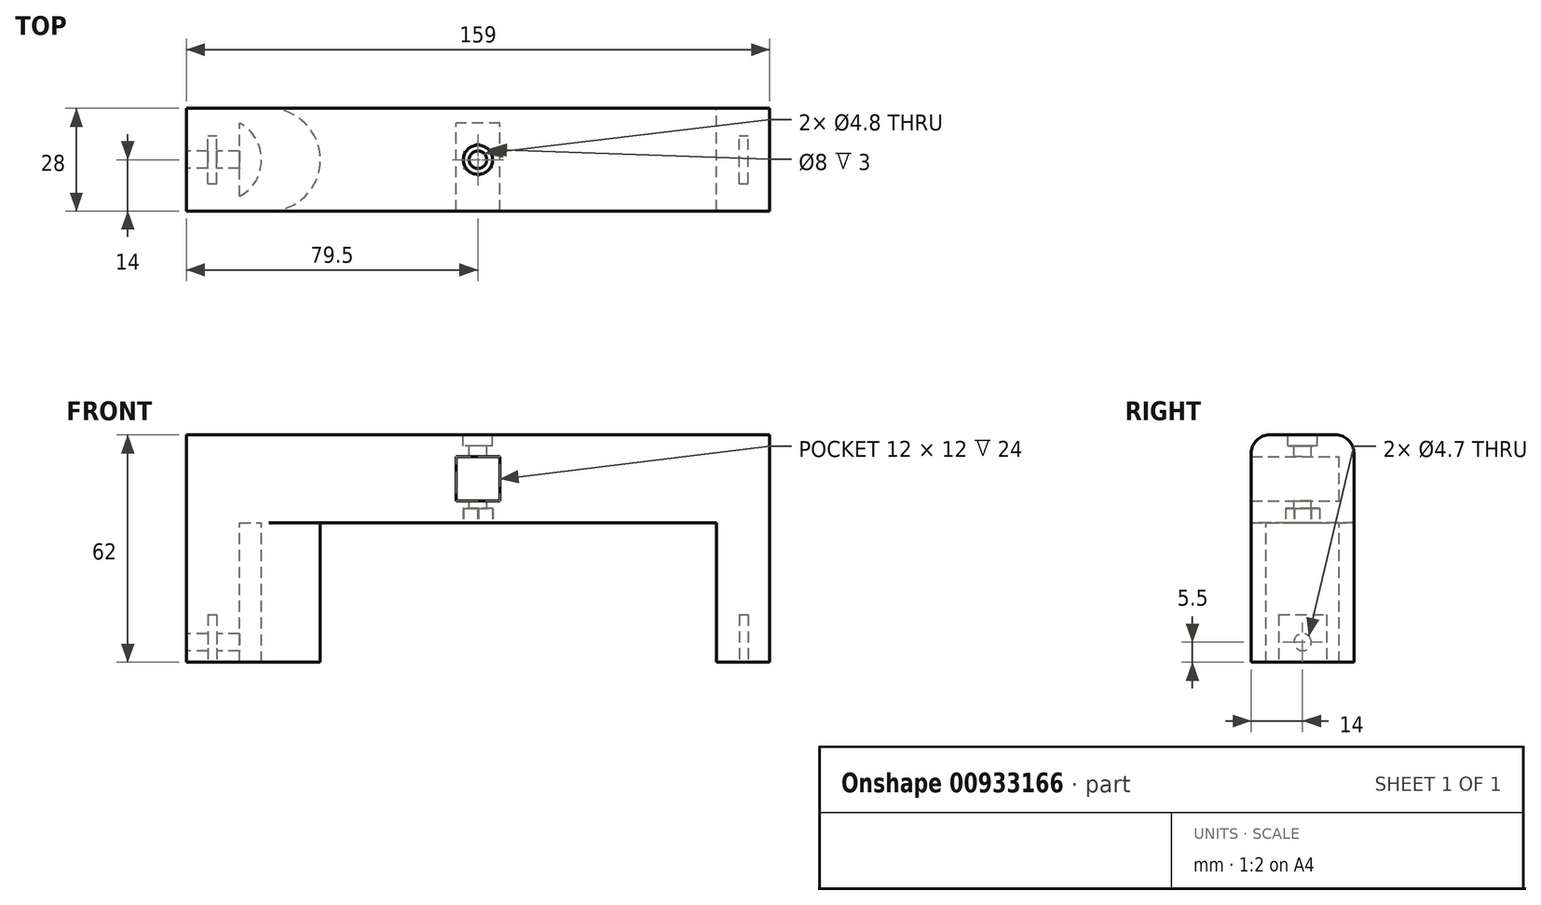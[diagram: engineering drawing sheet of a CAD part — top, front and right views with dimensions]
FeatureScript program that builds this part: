
annotation { "Feature Type Name" : "Feature", "Feature Type Description" : "" }
export const myFeature = defineFeature(function(context is Context, id is Id, definition is map)
    precondition{}
    {
        {
            var Q0;
            Q0=qCreatedBy(makeId("Front.planeOp"),FACE);
            var sketch = newSketch(context, id + "F0", { "sketchPlane" : qUnion([Q0])});
            skLineSegment(sketch, "E0.bottom", {"start": v(0, 0) * mm, "end": v(14.5, 0) * mm});
            skLineSegment(sketch, "E0.top", {"start": v(0, 62) * mm, "end": v(159, 62) * mm});
            skLineSegment(sketch, "E0.left", {"start": v(0, 0) * mm, "end": v(0, 62) * mm});
            skLineSegment(sketch, "E0.right", {"start": v(159, 0) * mm, "end": v(159, 62) * mm});
            skLineSegment(sketch, "E1.top", {"start": v(14.5, 38) * mm, "end": v(144.5, 38) * mm});
            skLineSegment(sketch, "E1.left", {"start": v(14.5, 0) * mm, "end": v(14.5, 38) * mm});
            skLineSegment(sketch, "E1.right", {"start": v(144.5, 0) * mm, "end": v(144.5, 38) * mm});
            skLineSegment(sketch, "E2.trimOffspring", {"start": v(144.5, 0) * mm, "end": v(159, 0) * mm});
            skLineSegment(sketch, "E3", {"start": v(79.5, 62) * mm, "end": v(79.5, 38) * mm, "construction": true});
            skLineSegment(sketch, "E4.bottom", {"start": v(85.5, 44) * mm, "end": v(73.5, 44) * mm});
            skLineSegment(sketch, "E4.top", {"start": v(85.5, 56) * mm, "end": v(73.5, 56) * mm});
            skLineSegment(sketch, "E4.left", {"start": v(85.5, 44) * mm, "end": v(85.5, 56) * mm});
            skLineSegment(sketch, "E4.right", {"start": v(73.5, 44) * mm, "end": v(73.5, 56) * mm});
            skPoint(sketch, "E4.middle", {"position": v(79.5, 50) * mm});
            skSolve(sketch);
        }
        {
            var Q0;
            Q0=makeQuery(id+"F0.imprint","IMPRINT",FACE,{"disambiguationData":[TD([[makeQuery(id+"F0.imprint","IMPRINT",EDGE,{"derivedFrom":sQuery(id+"F0.wireOp",EDGE,"E0.bottom")}),1.0]])]});
            extrude(context, id + "F1", {"entities" : qUnion([Q0]), "depth" : 28 * mm, "offsetDistance" : 25 * mm});
        }
        {
            var Q0;
            Q0=makeQuery(id+"F0.imprint","IMPRINT",FACE,{"disambiguationData":[TD([[makeQuery(id+"F0.imprint","IMPRINT",EDGE,{"derivedFrom":sQuery(id+"F0.wireOp",EDGE,"E4.bottom")}),-1.0]])]});
            extrude(context, id + "F2", {"entities" : qUnion([Q0]), "operationType" : NewBodyOperationType.ADD, "depth" : 4 * mm, "offsetDistance" : 25 * mm});
        }
        {
            var Q0;
            Q0=makeQuery(id+"F1.opExtrude","SWEPT_FACE",FACE,{"disambiguationData":[OSD([sQuery(id+"F0.wireOp",EDGE,"E0.bottom")])]});
            var sketch = newSketch(context, id + "F3", { "sketchPlane" : qUnion([Q0])});
            skLineSegment(sketch, "E5.bottom", {"start": v(5.8, 20.5) * mm, "end": v(8.2, 20.5) * mm});
            skLineSegment(sketch, "E5.top", {"start": v(5.8, 7.5) * mm, "end": v(8.2, 7.5) * mm});
            skLineSegment(sketch, "E5.left", {"start": v(5.8, 20.5) * mm, "end": v(5.8, 7.5) * mm});
            skLineSegment(sketch, "E5.right", {"start": v(8.2, 20.5) * mm, "end": v(8.2, 7.5) * mm});
            skLineSegment(sketch, "E6.bottom", {"start": v(150.8, 20.5) * mm, "end": v(153.2, 20.5) * mm});
            skLineSegment(sketch, "E6.top", {"start": v(150.8, 7.5) * mm, "end": v(153.2, 7.5) * mm});
            skLineSegment(sketch, "E6.left", {"start": v(150.8, 20.5) * mm, "end": v(150.8, 7.5) * mm});
            skLineSegment(sketch, "E6.right", {"start": v(153.2, 20.5) * mm, "end": v(153.2, 7.5) * mm});
            skPoint(sketch, "E7.0", {"position": v(0, 28) * mm});
            skPoint(sketch, "E8.0", {"position": v(159, 28) * mm});
            skLineSegment(sketch, "E9", {"start": v(0, 28) * mm, "end": v(159, 28) * mm, "construction": true});
            skLineSegment(sketch, "E10", {"start": v(79.5, 28) * mm, "end": v(79.5, -8.8) * mm, "construction": true});
            skLineSegment(sketch, "E11", {"start": v(7, 20.5) * mm, "end": v(7, 4.09) * mm, "construction": true});
            skLineSegment(sketch, "E12", {"start": v(152, 20.5) * mm, "end": v(152, 3.87) * mm, "construction": true});
            skPoint(sketch, "E13", {"position": v(0, 14) * mm});
            skPoint(sketch, "E14", {"position": v(5.8, 14) * mm});
            skPoint(sketch, "E15", {"position": v(8.2, 14) * mm});
            skLineSegment(sketch, "E16", {"start": v(9.59, 14) * mm, "end": v(-2.3, 14) * mm, "construction": true});
            skSolve(sketch);
        }
        {
            var Q0;
            Q0=qSketchRegion(id+"F3",true);
            extrude(context, id + "F4", {"entities" : qUnion([Q0]), "operationType" : NewBodyOperationType.REMOVE, "oppositeDirection" : true, "depth" : 13 * mm, "offsetDistance" : 25 * mm});
        }
        {
            var Q0;
            Q0=makeQuery(id+"F1.opExtrude","SWEPT_FACE",FACE,{"disambiguationData":[OSD([sQuery(id+"F0.wireOp",EDGE,"E0.left")])]});
            var sketch = newSketch(context, id + "F5", { "sketchPlane" : qUnion([Q0])});
            skPoint(sketch, "E17.0", {"position": v(14, 0) * mm});
            skLineSegment(sketch, "E18", {"start": v(14, 0) * mm, "end": v(14, 41.7) * mm, "construction": true});
            skCircle(sketch, "E19", {"center": v(14, 5.5) * mm, "radius": 2.35 * mm});
            skSolve(sketch);
        }
        {
            var Q0;
            Q0=qSketchRegion(id+"F5",true);
            var Q1;
            Q1=makeQuery(id+"F1.opExtrude","SWEPT_FACE",FACE,{"disambiguationData":[OSD([sQuery(id+"F0.wireOp",EDGE,"E1.left")])]});
            extrude(context, id + "F6", {"entities" : qUnion([Q0]), "operationType" : NewBodyOperationType.REMOVE, "oppositeDirection" : true, "depth" : 14.5 * mm, "endBoundEntityFace" : qUnion([Q1]), "offsetDistance" : 25 * mm});
        }
        {
            var Q0;
            Q0=makeQuery(id+"F1.opExtrude","CAP_VERTEX",VERTEX,{"disambiguationData":[OSD([sQuery(id+"F0.wireOp",EDGE,"E0.top"),sQuery(id+"F0.wireOp",EDGE,"E0.left")])],"isStart":false});
            var Q1;
            Q1=makeQuery(id+"F1.opExtrude","CAP_VERTEX",VERTEX,{"disambiguationData":[OSD([sQuery(id+"F0.wireOp",EDGE,"E0.top"),sQuery(id+"F0.wireOp",EDGE,"E0.right")])],"isStart":false});
            cPlane(context, id + "F7", {"entities" : qUnion([Q0, Q1]), "cplaneType" : CPlaneType.MID_PLANE, "offset" : 25 * mm, "width" : 150 * mm, "height" : 150 * mm});
        }
        {
            var Q0;
            Q0=makeQuery(id+"F1.opExtrude","SWEPT_FACE",FACE,{"disambiguationData":[OSD([sQuery(id+"F0.wireOp",EDGE,"E1.top")])]});
            var sketch = newSketch(context, id + "F8", { "sketchPlane" : qUnion([Q0])});
            skPoint(sketch, "E20", {"position": v(14.5, 24) * mm});
            skPoint(sketch, "E21", {"position": v(14.5, 4) * mm});
            skPoint(sketch, "E22", {"position": v(20.5, 14) * mm});
            skPoint(sketch, "E22.positionSnap0", {"position": v(14.5, 14) * mm});
            skArc(sketch, "E23", {"start": v(14.5, 4) * mm, "mid": v(20.5, 14) * mm, "end": v(14.5, 24) * mm});
            skLineSegment(sketch, "E24", {"start": v(14.5, 0) * mm, "end": v(14.5, 4) * mm});
            skLineSegment(sketch, "E25", {"start": v(14.5, 24) * mm, "end": v(14.5, 28) * mm});
            skArc(sketch, "E26", {"start": v(22.5, 28) * mm, "mid": v(36.5, 14) * mm, "end": v(22.5, 0) * mm});
            skLineSegment(sketch, "E27", {"start": v(14.5, 28) * mm, "end": v(22.5, 28) * mm});
            skLineSegment(sketch, "E28", {"start": v(22.5, 0) * mm, "end": v(14.5, 0) * mm});
            skLineSegment(sketch, "E29", {"start": v(79.5, 28) * mm, "end": v(79.5, 0) * mm, "construction": true});
            skPoint(sketch, "E30", {"position": v(79.5, 14) * mm});
            skCircle(sketch, "E31.cCircle", {"center": v(79.5, 14) * mm, "radius": 4.6 * mm, "construction": true});
            skLineSegment(sketch, "E31.0", {"start": v(83.53, 11.78) * mm, "end": v(79.6, 9.4) * mm});
            skLineSegment(sketch, "E31.1", {"start": v(79.6, 9.4) * mm, "end": v(75.56, 11.62) * mm});
            skLineSegment(sketch, "E31.2", {"start": v(75.56, 11.62) * mm, "end": v(75.47, 16.22) * mm});
            skLineSegment(sketch, "E31.3", {"start": v(75.47, 16.22) * mm, "end": v(79.4, 18.6) * mm});
            skLineSegment(sketch, "E31.4", {"start": v(79.4, 18.6) * mm, "end": v(83.44, 16.38) * mm});
            skLineSegment(sketch, "E31.5", {"start": v(83.44, 16.38) * mm, "end": v(83.53, 11.78) * mm});
            skSolve(sketch);
        }
        {
            var Q0;
            Q0=makeQuery(id+"F8.imprint","IMPRINT",FACE,{"disambiguationData":[TD([[makeQuery(id+"F8.imprint","IMPRINT",EDGE,{"derivedFrom":sQuery(id+"F8.wireOp",EDGE,"E23")}),-1.0]])]});
            var Q1;
            Q1=makeQuery(id+"F1.opExtrude","SWEPT_FACE",FACE,{"disambiguationData":[OSD([sQuery(id+"F0.wireOp",EDGE,"E0.bottom")])]});
            extrude(context, id + "F9", {"entities" : qUnion([Q0]), "operationType" : NewBodyOperationType.ADD, "endBound" : BoundingType.UP_TO_SURFACE, "depth" : 25 * mm, "endBoundEntityFace" : qUnion([Q1]), "offsetDistance" : 25 * mm});
        }
        {
            var Q0;
            Q0=makeQuery(id+"F1.opExtrude","SWEPT_FACE",FACE,{"disambiguationData":[OSD([sQuery(id+"F0.wireOp",EDGE,"E0.top")])]});
            var sketch = newSketch(context, id + "F10", { "sketchPlane" : qUnion([Q0])});
            skPoint(sketch, "E32.positionSnap0", {"position": v(79.5, -28) * mm});
            skPoint(sketch, "E33", {"position": v(79.5, -14) * mm});
            skPoint(sketch, "E33.positionSnap0", {"position": v(159, -14) * mm});
            skSolve(sketch);
        }
        {
            var Q0;
            Q0=sQuery(id+"F10.wireOp",VERTEX,"E33");
            var Q1;
            Q1=makeQuery(id+"F1.opExtrude","SWEPT_BODY",BODY,{"disambiguationData":[OSD([sQuery(id+"F0.wireOp",EDGE,"E0.bottom"),sQuery(id+"F0.wireOp",EDGE,"E0.top"),sQuery(id+"F0.wireOp",EDGE,"E0.left"),sQuery(id+"F0.wireOp",EDGE,"E0.right"),sQuery(id+"F0.wireOp",EDGE,"E1.top"),sQuery(id+"F0.wireOp",EDGE,"E1.left"),sQuery(id+"F0.wireOp",EDGE,"E1.right"),sQuery(id+"F0.wireOp",EDGE,"E2.trimOffspring"),sQuery(id+"F0.wireOp",EDGE,"E4.bottom"),sQuery(id+"F0.wireOp",EDGE,"E4.top"),sQuery(id+"F0.wireOp",EDGE,"E4.left"),sQuery(id+"F0.wireOp",EDGE,"E4.right")])]});
            hole(context, id + "F11", {"style" : HoleStyle.C_BORE, "endStyle" : HoleEndStyle.THROUGH, "holeDiameter" : 4.8 * mm, "cBoreDiameter" : 8 * mm, "cBoreDepth" : 3 * mm, "majorDiameter" : 5 * mm, "isTappedThrough" : true, "tappedDepth" : 12 * mm, "tapClearance" : 3, "locations" : qUnion([Q0]), "scope" : qUnion([Q1])});
        }
        {
            var Q0;
            Q0=makeQuery(id+"F8.imprint","IMPRINT",FACE,{"disambiguationData":[TD([[makeQuery(id+"F8.imprint","IMPRINT",EDGE,{"derivedFrom":sQuery(id+"F8.wireOp",EDGE,"E31.0")}),-1.0]])]});
            extrude(context, id + "F12", {"entities" : qUnion([Q0]), "operationType" : NewBodyOperationType.REMOVE, "oppositeDirection" : true, "depth" : 4 * mm, "offsetDistance" : 25 * mm});
        }
        {
            var Q0;
            Q0=makeQuery(id+"F1.opExtrude","CAP_EDGE",EDGE,{"disambiguationData":[OSD([sQuery(id+"F0.wireOp",EDGE,"E0.top")])],"isStart":false});
            var Q1;
            Q1=makeQuery(id+"F1.opExtrude","CAP_EDGE",EDGE,{"disambiguationData":[OSD([sQuery(id+"F0.wireOp",EDGE,"E0.top")])],"isStart":true});
            fillet(context, id + "F13", {"entities" : qUnion([Q0, Q1]), "radius" : 5 * mm, "tangentPropagation" : true, "allowEdgeOverflow" : false});
        }
    });
